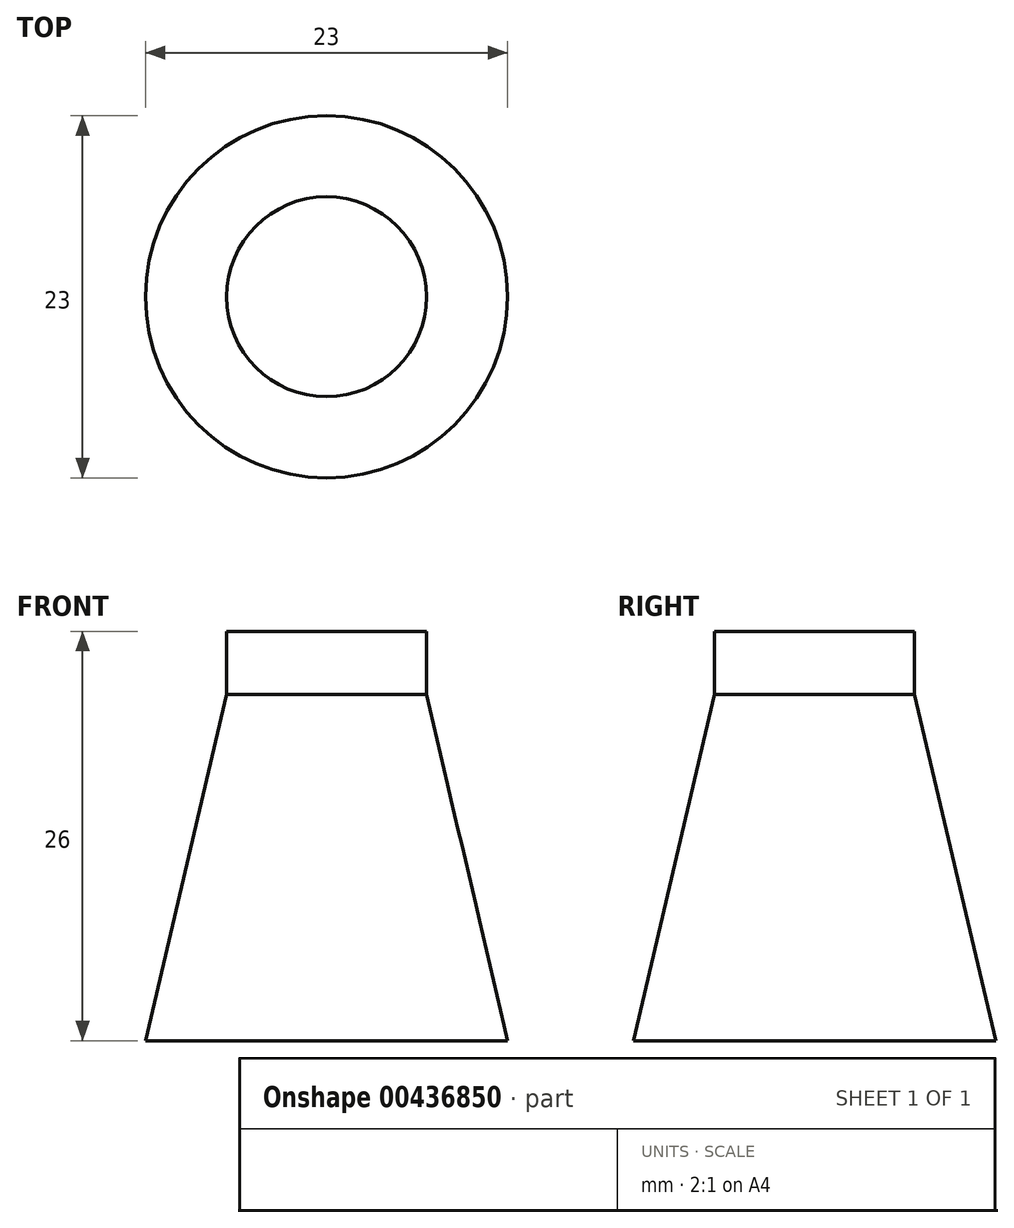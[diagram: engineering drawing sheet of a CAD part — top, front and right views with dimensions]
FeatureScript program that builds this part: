
annotation { "Feature Type Name" : "Feature", "Feature Type Description" : "" }
export const myFeature = defineFeature(function(context is Context, id is Id, definition is map)
    precondition{}
    {
        {
            var Q0;
            Q0=qCreatedBy(makeId("Right.planeOp"),FACE);
            var sketch = newSketch(context, id + "F0", { "sketchPlane" : qUnion([Q0])});
            skLineSegment(sketch, "E0", {"start": v(0, 0) * mm, "end": v(11.5, 0) * mm});
            skLineSegment(sketch, "E1", {"start": v(6.35, 22) * mm, "end": v(11.5, 0) * mm});
            skLineSegment(sketch, "E2", {"start": v(6.35, 22) * mm, "end": v(6.35, 26) * mm});
            skLineSegment(sketch, "E3", {"start": v(6.35, 26) * mm, "end": v(0, 26) * mm});
            skLineSegment(sketch, "E4", {"start": v(0, 26) * mm, "end": v(0, 0) * mm});
            skSolve(sketch);
        }
        {
            var Q0;
            Q0=qSketchRegion(id+"F0",true);
            var Q1;
            Q1=sQuery(id+"F0.wireOp",EDGE,"E4");
            revolve(context, id + "F1", {"entities" : qUnion([Q0]), "axis" : qUnion([Q1]), "revolveType" : RevolveType.FULL});
        }
    });
